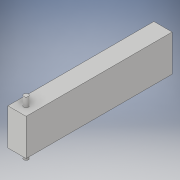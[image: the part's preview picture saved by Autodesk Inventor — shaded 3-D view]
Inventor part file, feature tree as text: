
AUTODESK INVENTOR PART (.ipt)
format: ipt  version: 2017 (Build 210142000, 142)  size: 107,520 bytes
history: native  units: in
note: dims shown in document units (in); Inventor stores cm internally (conversion verified against a paired STEP export)
features: extrude x3, sketch x3, projected_geometry x2
ambient origin geometry x8: Origin, YZ Plane, XZ Plane, XY Plane, X Axis, Y Axis, Z Axis, Center Point
bodies: Solid1 (feature_tree)
feature tree (8):
  extrude  "Extrusion1"  Depth=8.0in
  extrude  "Extrusion2"  Depth=1.0in
  extrude  "Extrusion3"  Depth=0.5in
  sketch  "Sketch1"  dims[d0=2.0in d1=8.0in]
  sketch  "Sketch2"  dims[d2=1.0in d3=0.0in d4=0.25in]
  projected_geometry  "Projected Loop1"
  sketch  "Sketch3"  dims[d5=0.5in d6=0.5in d7=0.5in d8=0.0in d9=0.25in d10=0.5in d11=0.5in d12=0.5in d13=0.0in]
  projected_geometry  "Projected Loop2"
